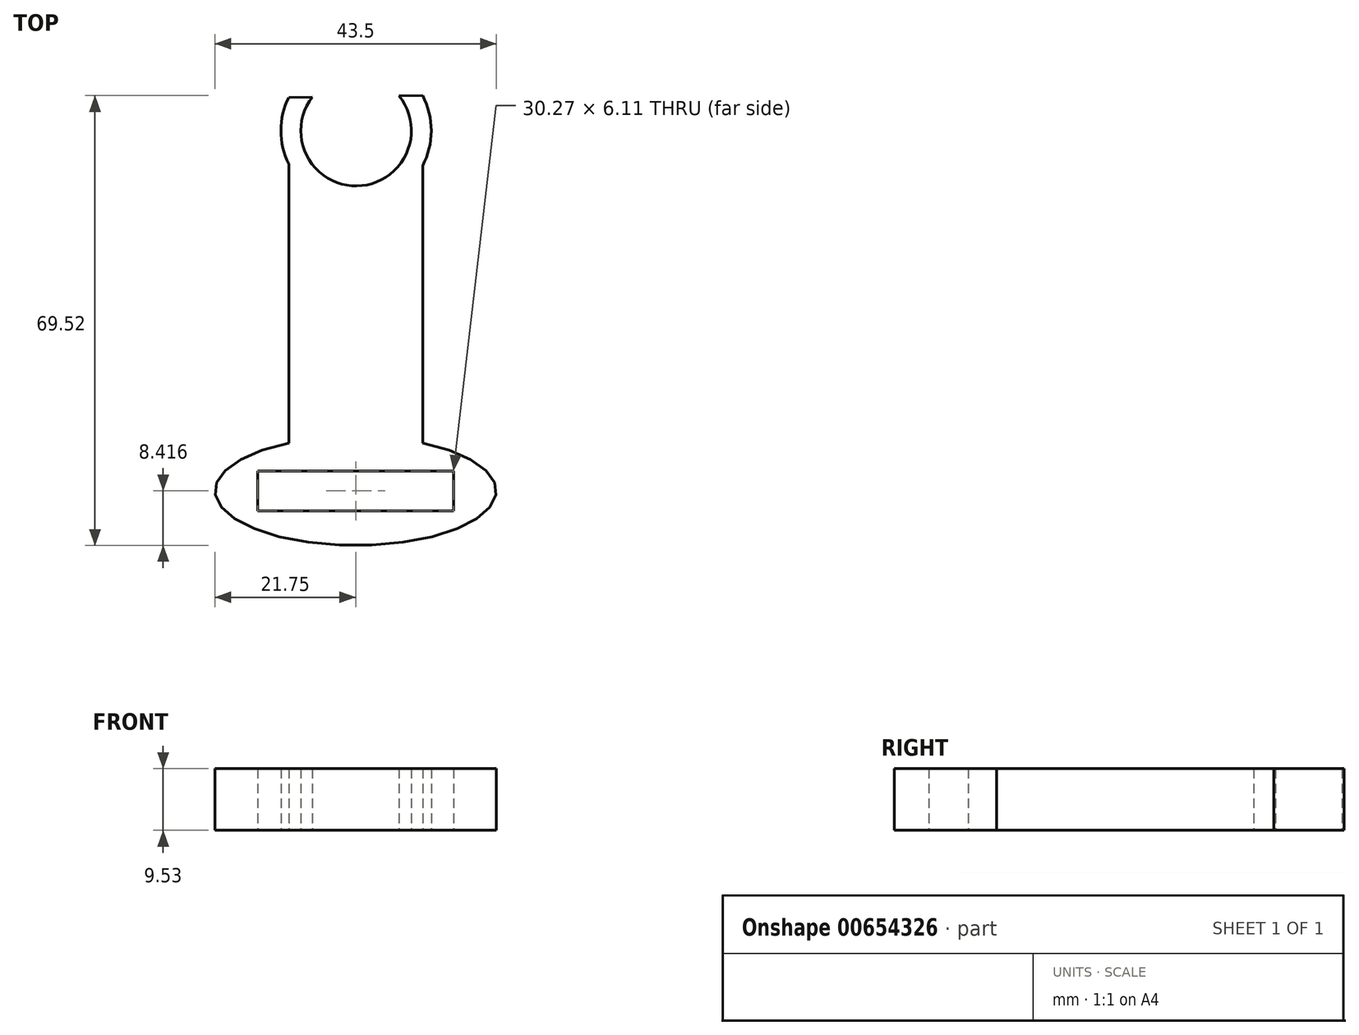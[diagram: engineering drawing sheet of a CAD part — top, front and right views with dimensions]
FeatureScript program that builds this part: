
annotation { "Feature Type Name" : "Feature", "Feature Type Description" : "" }
export const myFeature = defineFeature(function(context is Context, id is Id, definition is map)
    precondition{}
    {
        {
            var Q0;
            Q0=qCreatedBy(makeId("Top.planeOp"),FACE);
            var sketch = newSketch(context, id + "F0", { "sketchPlane" : qUnion([Q0])});
            skLineSegment(sketch, "E0.bottom", {"start": v(-10.35, 26.3) * mm, "end": v(10.35, 26.3) * mm});
            skLineSegment(sketch, "E0.top", {"start": v(-10.35, -26.3) * mm, "end": v(10.35, -26.3) * mm});
            skLineSegment(sketch, "E0.left", {"start": v(-10.35, 26.3) * mm, "end": v(-10.35, -26.3) * mm});
            skLineSegment(sketch, "E0.right", {"start": v(10.35, 26.3) * mm, "end": v(10.35, -26.3) * mm});
            skPoint(sketch, "E0.middle", {"position": v(0, 0) * mm});
            skArc(sketch, "E1", {"start": v(-10.35, 34.63) * mm, "mid": v(0.23, 17.85) * mm, "end": v(10.35, 34.9) * mm});
            skEllipse(sketch, "E2", {"center": v(0, -26.2) * mm, "majorRadius": 21.75 * mm, "minorRadius": 8.42 * mm, "majorAxis": v(-1, 0)});
            skPoint(sketch, "E2.centerSnap0", {"position": v(0, -26.3) * mm});
            skLineSegment(sketch, "E3", {"start": v(-10.35, 34.63) * mm, "end": v(10.35, 34.9) * mm});
            skCircle(sketch, "E4", {"center": v(0.07, 29.47) * mm, "radius": 8.54 * mm});
            skLineSegment(sketch, "E5.bottom", {"start": v(-15.14, -23.15) * mm, "end": v(15.14, -23.15) * mm});
            skLineSegment(sketch, "E5.top", {"start": v(-15.14, -29.26) * mm, "end": v(15.14, -29.26) * mm});
            skLineSegment(sketch, "E5.left", {"start": v(-15.14, -23.15) * mm, "end": v(-15.14, -29.26) * mm});
            skLineSegment(sketch, "E5.right", {"start": v(15.14, -23.15) * mm, "end": v(15.14, -29.26) * mm});
            skSolve(sketch);
        }
        {
            var Q0;
            {var subQ5=sQuery(id+"F0.wireOp",EDGE,"E0.left");var subQ7=sQuery(id+"F0.wireOp",EDGE,"E0.bottom");var subQ8=makeQuery(id+"F0.imprint","INTERSECT",VERTEX,{"derivedFrom":[subQ7,subQ5]});Q0=makeQuery(id+"F0.imprint","IMPRINT",FACE,{"disambiguationData":[TD([[makeQuery(id+"F0.imprint","IMPRINT",EDGE,{"disambiguationData":[TD([[subQ8,-1.0]])],"derivedFrom":subQ7}),1.0]])]});}
            var Q1;
            {var subQ1=sQuery(id+"F0.wireOp",EDGE,"E0.bottom");var subQ5=sQuery(id+"F0.wireOp",EDGE,"E0.left");var subQ6=makeQuery(id+"F0.imprint","INTERSECT",VERTEX,{"derivedFrom":[subQ1,subQ5]});Q1=makeQuery(id+"F0.imprint","IMPRINT",FACE,{"disambiguationData":[TD([[makeQuery(id+"F0.imprint","IMPRINT",EDGE,{"disambiguationData":[TD([[subQ6,-1.0]])],"derivedFrom":subQ1}),-1.0]])]});}
            var Q2;
            {var subQ5=sQuery(id+"F0.wireOp",EDGE,"E0.right");var subQ6=sQuery(id+"F0.wireOp",EDGE,"E0.bottom");var subQ7=makeQuery(id+"F0.imprint","INTERSECT",VERTEX,{"derivedFrom":[subQ6,subQ5]});Q2=makeQuery(id+"F0.imprint","IMPRINT",FACE,{"disambiguationData":[TD([[makeQuery(id+"F0.imprint","IMPRINT",EDGE,{"disambiguationData":[TD([[subQ7,1.0]])],"derivedFrom":subQ6}),1.0]])]});}
            var Q3;
            {var subQ0=sQuery(id+"F0.wireOp",EDGE,"E1");var subQ1=sQuery(id+"F0.wireOp",EDGE,"E0.left");var subQ2=makeQuery(id+"F0.imprint","INTERSECT",VERTEX,{"derivedFrom":[subQ1,subQ0]});Q3=makeQuery(id+"F0.imprint","IMPRINT",FACE,{"disambiguationData":[TD([[makeQuery(id+"F0.imprint","IMPRINT",EDGE,{"disambiguationData":[TD([[subQ2,-1.0]])],"derivedFrom":subQ1}),1.0]])]});}
            var Q4;
            Q4=makeQuery(id+"F0.imprint","IMPRINT",FACE,{"disambiguationData":[TD([[makeQuery(id+"F0.imprint","IMPRINT",EDGE,{"derivedFrom":sQuery(id+"F0.wireOp",EDGE,"E5.top")}),-1.0]])]});
            var Q5;
            {var subQ0=sQuery(id+"F0.wireOp",EDGE,"E2");var subQ1=sQuery(id+"F0.wireOp",EDGE,"E0.left");var subQ2=makeQuery(id+"F0.imprint","INTERSECT",VERTEX,{"derivedFrom":[subQ1,subQ0]});Q5=makeQuery(id+"F0.imprint","IMPRINT",FACE,{"disambiguationData":[TD([[makeQuery(id+"F0.imprint","IMPRINT",EDGE,{"disambiguationData":[TD([[subQ2,-1.0]])],"derivedFrom":subQ1}),1.0]])]});}
            extrude(context, id + "F1", {"entities" : qUnion([Q0, Q1, Q2, Q3, Q4, Q5]), "depth" : 9.52 * mm, "offsetDistance" : 25.4 * mm});
        }
    });
